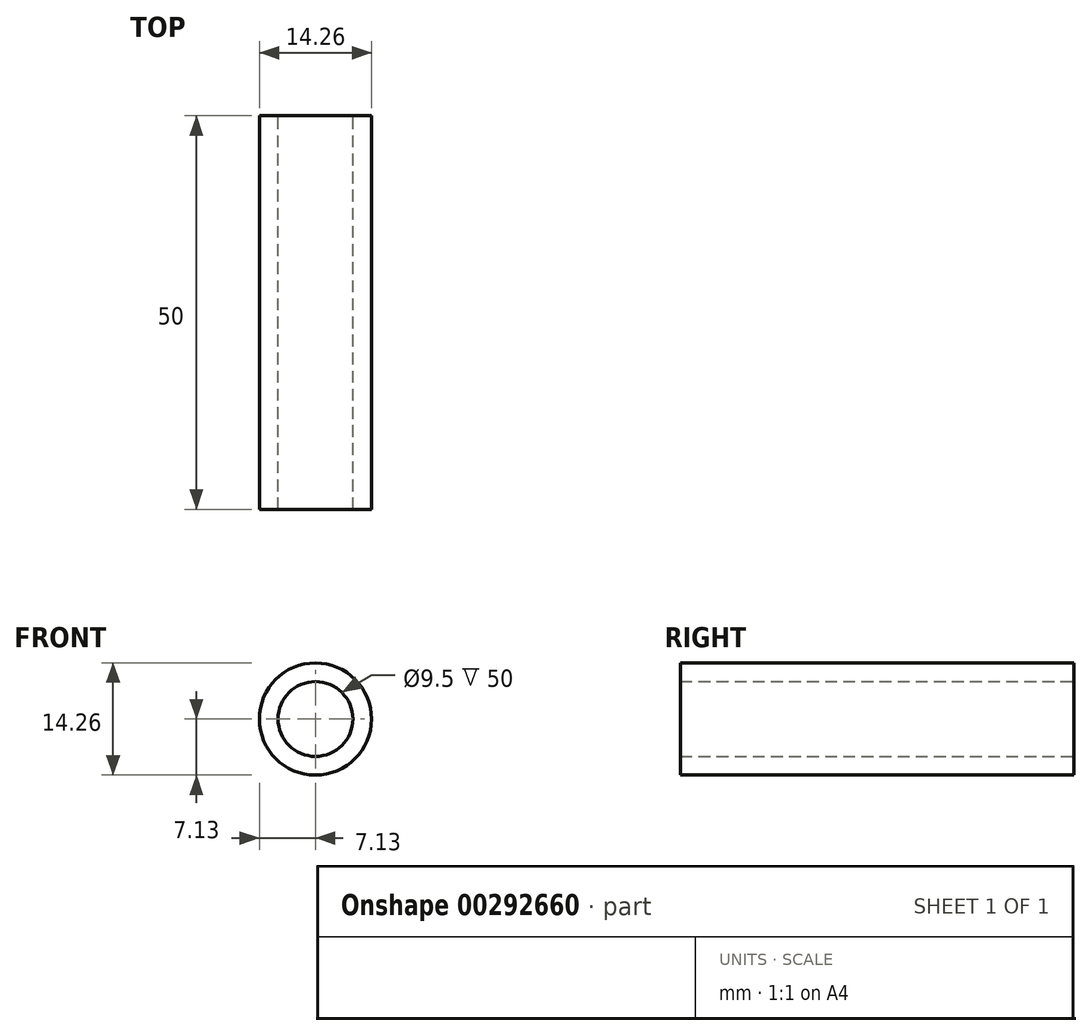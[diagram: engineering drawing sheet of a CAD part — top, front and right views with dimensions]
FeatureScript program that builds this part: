
annotation { "Feature Type Name" : "Feature", "Feature Type Description" : "" }
export const myFeature = defineFeature(function(context is Context, id is Id, definition is map)
    precondition{}
    {
        {
            var Q0;
            Q0=qCreatedBy(makeId("Front.planeOp"),FACE);
            var sketch = newSketch(context, id + "F0", { "sketchPlane" : qUnion([Q0])});
            skCircle(sketch, "E0", {"center": v(0, 0) * mm, "radius": 7.12 * mm});
            skCircle(sketch, "E1", {"center": v(0, 0) * mm, "radius": 4.75 * mm});
            skSolve(sketch);
        }
        {
            var Q0;
            Q0=makeQuery(id+"F0.imprint","IMPRINT",FACE,{"disambiguationData":[TD([[makeQuery(id+"F0.imprint","IMPRINT",EDGE,{"derivedFrom":sQuery(id+"F0.wireOp",EDGE,"E0")}),1.0]])]});
            extrude(context, id + "F1", {"entities" : qUnion([Q0]), "depth" : 50 * mm, "offsetDistance" : 25 * mm});
        }
    });
